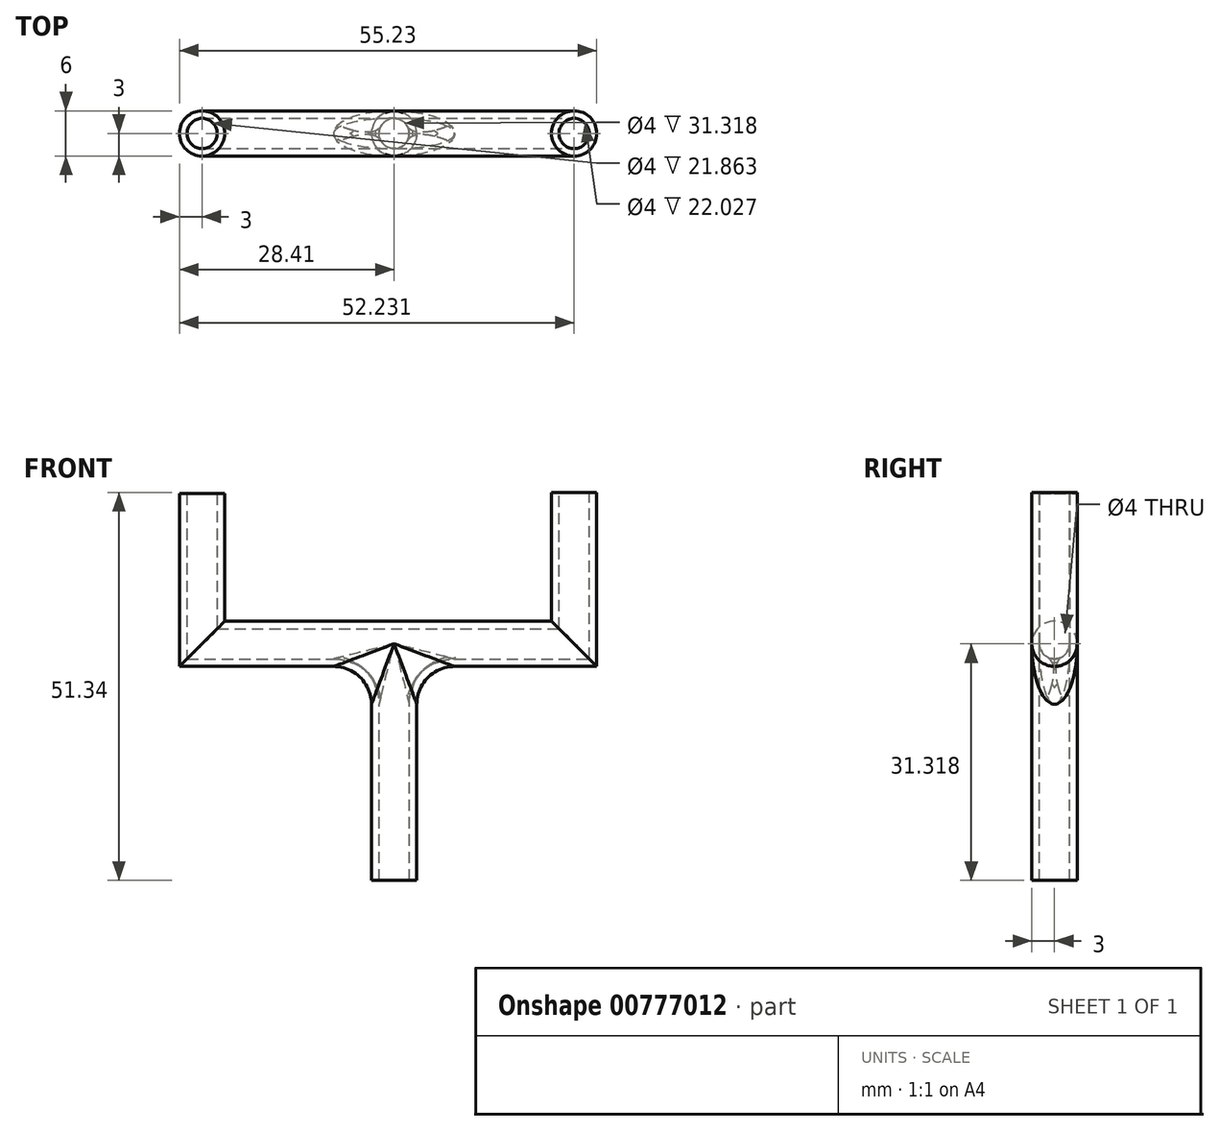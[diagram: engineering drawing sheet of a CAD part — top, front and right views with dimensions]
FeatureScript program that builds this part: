
annotation { "Feature Type Name" : "Feature", "Feature Type Description" : "" }
export const myFeature = defineFeature(function(context is Context, id is Id, definition is map)
    precondition{}
    {
        {
            var Q0;
            Q0=qCreatedBy(makeId("Front.planeOp"),FACE);
            var sketch = newSketch(context, id + "F0", { "sketchPlane" : qUnion([Q0])});
            skLineSegment(sketch, "E0", {"start": v(0, 0) * mm, "end": v(0, 31.32) * mm});
            skLineSegment(sketch, "E1", {"start": v(0, 31.32) * mm, "end": v(23.82, 31.32) * mm});
            skLineSegment(sketch, "E2", {"start": v(23.82, 31.32) * mm, "end": v(23.82, 51.34) * mm});
            skLineSegment(sketch, "E3", {"start": v(0, 31.32) * mm, "end": v(-25.4, 31.32) * mm});
            skLineSegment(sketch, "E4", {"start": v(-25.4, 31.32) * mm, "end": v(-25.4, 51.17) * mm});
            skSolve(sketch);
        }
        {
            var Q0;
            Q0=qCreatedBy(makeId("Top.planeOp"),FACE);
            var sketch = newSketch(context, id + "F1", { "sketchPlane" : qUnion([Q0])});
            skCircle(sketch, "E5", {"center": v(0, 0) * mm, "radius": 3 * mm});
            skSolve(sketch);
        }
        {
            var Q0;
            Q0=makeQuery(id+"F1.imprint","IMPRINT",FACE,{"disambiguationData":[TD([[makeQuery(id+"F1.imprint","IMPRINT",EDGE,{"derivedFrom":sQuery(id+"F1.wireOp",EDGE,"E5")}),1.0]])]});
            var Q1;
            Q1=sQuery(id+"F0.wireOp",EDGE,"E0");
            sweep(context, id + "F2", {"profiles" : qUnion([Q0]), "path" : qUnion([Q1])});
        }
        {
            var Q0;
            Q0=qCreatedBy(makeId("Top.planeOp"),FACE);
            var Q1;
            Q1=sQuery(id+"F0.wireOp",VERTEX,"E4.end");
            cPlane(context, id + "F3", {"entities" : qUnion([Q0, Q1]), "cplaneType" : CPlaneType.PLANE_POINT, "offset" : 25 * mm, "width" : 150 * mm, "height" : 150 * mm});
        }
        {
            var Q0;
            Q0=qCreatedBy(id+"F3.planeOp",FACE);
            var sketch = newSketch(context, id + "F4", { "sketchPlane" : qUnion([Q0])});
            skCircle(sketch, "E6", {"center": v(-25.4, 0) * mm, "radius": 3 * mm});
            skSolve(sketch);
        }
        {
            var Q0;
            Q0=makeQuery(id+"F4.imprint","IMPRINT",FACE,{"disambiguationData":[TD([[makeQuery(id+"F4.imprint","IMPRINT",EDGE,{"derivedFrom":sQuery(id+"F4.wireOp",EDGE,"E6")}),1.0]])]});
            var Q1;
            Q1=sQuery(id+"F0.wireOp",EDGE,"E4");
            var Q2;
            Q2=sQuery(id+"F0.wireOp",EDGE,"E3");
            var Q3;
            Q3=sQuery(id+"F0.wireOp",EDGE,"E1");
            var Q4;
            Q4=sQuery(id+"F0.wireOp",EDGE,"E2");
            sweep(context, id + "F5", {"operationType" : NewBodyOperationType.ADD, "profiles" : qUnion([Q0]), "path" : qUnion([Q1, Q2, Q3, Q4])});
        }
        {
            var Q0;
            Q0=makeQuery(id+"F5.boolean.opBoolean","INTERSECT",EDGE,{"disambiguationData":[OD(1.0)],"derivedFrom":[makeQuery(id+"F2.opSweep","SWEPT_FACE",FACE,{"disambiguationData":[OSD([sQuery(id+"F0.wireOp",EDGE,"E0"),sQuery(id+"F1.wireOp",EDGE,"E5")])]}),makeQuery(id+"F5.opSweep","SWEPT_FACE",FACE,{"disambiguationData":[OSD([sQuery(id+"F0.wireOp",EDGE,"E1"),sQuery(id+"F4.wireOp",EDGE,"E6")])]})]});
            var Q1;
            Q1=makeQuery(id+"F5.boolean.opBoolean","INTERSECT",EDGE,{"disambiguationData":[OD(0.0)],"derivedFrom":[makeQuery(id+"F2.opSweep","SWEPT_FACE",FACE,{"disambiguationData":[OSD([sQuery(id+"F0.wireOp",EDGE,"E0"),sQuery(id+"F1.wireOp",EDGE,"E5")])]}),makeQuery(id+"F5.opSweep","SWEPT_FACE",FACE,{"disambiguationData":[OSD([sQuery(id+"F0.wireOp",EDGE,"E1"),sQuery(id+"F4.wireOp",EDGE,"E6")])]})]});
            fillet(context, id + "F6", {"entities" : qUnion([Q0, Q1]), "radius" : 5 * mm, "tangentPropagation" : true, "allowEdgeOverflow" : false});
        }
        {
            var Q0;
            Q0=makeQuery(id+"F2.opSweep","CAP_FACE",FACE,{"disambiguationData":[OSD([sQuery(id+"F0.wireOp",VERTEX,"E0.start"),sQuery(id+"F1.wireOp",EDGE,"E5")])],"isStart":true});
            var Q1;
            Q1=makeQuery(id+"F5.opSweep","CAP_FACE",FACE,{"disambiguationData":[OSD([sQuery(id+"F0.wireOp",VERTEX,"E4.end"),sQuery(id+"F4.wireOp",EDGE,"E6")])],"isStart":true});
            var Q2;
            Q2=makeQuery(id+"F5.opSweep","CAP_FACE",FACE,{"disambiguationData":[OSD([sQuery(id+"F0.wireOp",VERTEX,"E2.end"),sQuery(id+"F4.wireOp",EDGE,"E6")])],"isStart":false});
            shell(context, id + "F7", {"entities" : qUnion([Q0, Q1, Q2]), "thickness" : 1 * mm});
        }
    });
